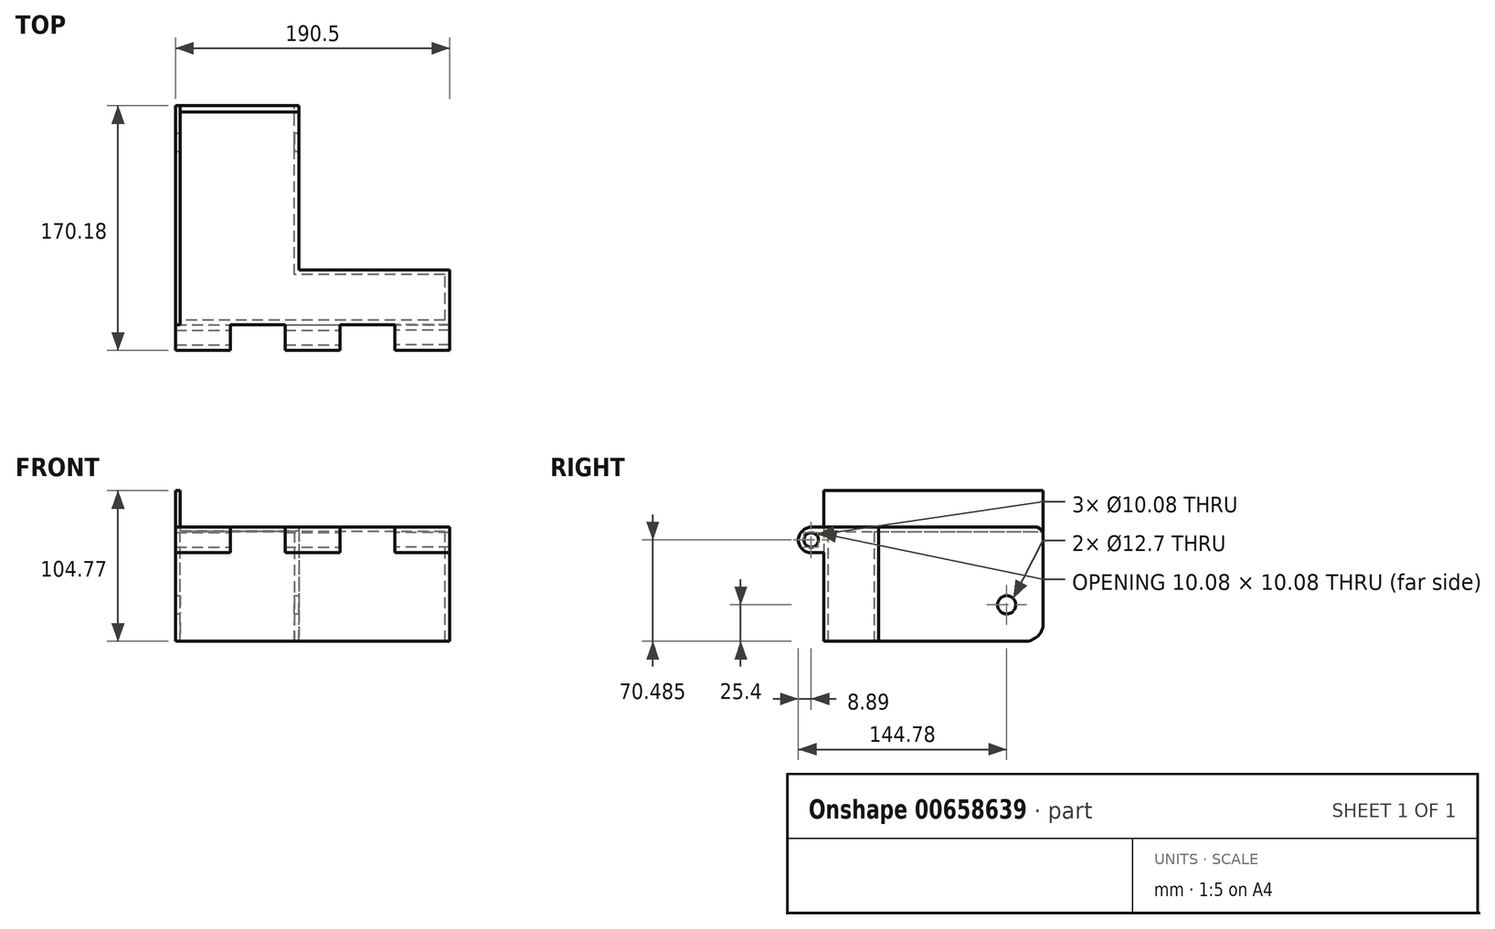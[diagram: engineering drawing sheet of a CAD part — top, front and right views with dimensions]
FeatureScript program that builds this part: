
annotation { "Feature Type Name" : "Feature", "Feature Type Description" : "" }
export const myFeature = defineFeature(function(context is Context, id is Id, definition is map)
    precondition{}
    {
        {
            var Q0;
            Q0=qCreatedBy(makeId("Front.planeOp"),FACE);
            var sketch = newSketch(context, id + "F0", { "sketchPlane" : qUnion([Q0])});
            skLineSegment(sketch, "E0.bottom", {"start": v(0, 0) * mm, "end": v(3.18, 0) * mm});
            skLineSegment(sketch, "E0.top", {"start": v(0, 76.2) * mm, "end": v(3.17, 76.2) * mm});
            skLineSegment(sketch, "E0.left", {"start": v(0, 0) * mm, "end": v(0, 76.2) * mm});
            skLineSegment(sketch, "E0.right", {"start": v(3.18, 0) * mm, "end": v(3.17, 76.2) * mm});
            skLineSegment(sketch, "E1.bottom", {"start": v(3.17, 76.2) * mm, "end": v(82.55, 76.2) * mm});
            skLineSegment(sketch, "E1.top", {"start": v(3.17, 79.38) * mm, "end": v(82.55, 79.38) * mm});
            skLineSegment(sketch, "E1.left", {"start": v(3.17, 76.2) * mm, "end": v(3.17, 79.38) * mm});
            skLineSegment(sketch, "E1.right", {"start": v(82.55, 76.2) * mm, "end": v(82.55, 79.38) * mm});
            skLineSegment(sketch, "E2.bottom", {"start": v(82.55, 76.2) * mm, "end": v(85.72, 76.2) * mm});
            skLineSegment(sketch, "E2.top", {"start": v(82.55, 0) * mm, "end": v(85.72, 0) * mm});
            skLineSegment(sketch, "E2.left", {"start": v(82.55, 76.2) * mm, "end": v(82.55, 0) * mm});
            skLineSegment(sketch, "E2.right", {"start": v(85.72, 76.2) * mm, "end": v(85.72, 0) * mm});
            skLineSegment(sketch, "E3.top", {"start": v(0, 79.38) * mm, "end": v(3.17, 79.38) * mm});
            skLineSegment(sketch, "E3.left", {"start": v(0, 76.2) * mm, "end": v(0, 79.38) * mm});
            skLineSegment(sketch, "E4.bottom", {"start": v(85.72, 76.2) * mm, "end": v(82.55, 76.2) * mm});
            skLineSegment(sketch, "E4.top", {"start": v(85.72, 79.38) * mm, "end": v(82.55, 79.38) * mm});
            skLineSegment(sketch, "E4.left", {"start": v(85.72, 76.2) * mm, "end": v(85.72, 79.38) * mm});
            skSolve(sketch);
        }
        {
            var Q0;
            Q0 = qSketchRegion(id + "F0", true);
            extrude(context, id + "F1", {"entities" : qUnion([Q0]), "depth" : 152.4 * mm, "offsetDistance" : 25.4 * mm});
        }
        {
            var Q0;
            Q0=makeQuery(id+"F1.opExtrude","SWEPT_FACE",FACE,{"disambiguationData":[OSD([sQuery(id+"F0.wireOp",EDGE,"E2.right"),sQuery(id+"F0.wireOp",EDGE,"E4.left")])]});
            var sketch = newSketch(context, id + "F2", { "sketchPlane" : qUnion([Q0])});
            skLineSegment(sketch, "E5.bottom", {"start": v(-152.4, 0) * mm, "end": v(-149.22, 0) * mm});
            skLineSegment(sketch, "E5.top", {"start": v(-152.4, 79.38) * mm, "end": v(-149.22, 79.38) * mm});
            skLineSegment(sketch, "E5.left", {"start": v(-152.4, 0) * mm, "end": v(-152.4, 79.38) * mm});
            skLineSegment(sketch, "E5.right", {"start": v(-149.22, 0) * mm, "end": v(-149.22, 79.38) * mm});
            skLineSegment(sketch, "E6", {"start": v(-152.4, 79.38) * mm, "end": v(-114.3, 79.38) * mm});
            skLineSegment(sketch, "E7.bottom", {"start": v(-114.3, 79.38) * mm, "end": v(-117.48, 79.38) * mm});
            skLineSegment(sketch, "E7.top", {"start": v(-114.3, 0) * mm, "end": v(-117.47, 0) * mm});
            skLineSegment(sketch, "E7.left", {"start": v(-114.3, 79.38) * mm, "end": v(-114.3, 0) * mm});
            skLineSegment(sketch, "E7.right", {"start": v(-117.48, 79.38) * mm, "end": v(-117.47, 0) * mm});
            skLineSegment(sketch, "E8.top", {"start": v(-152.4, 76.2) * mm, "end": v(-114.3, 76.2) * mm});
            skLineSegment(sketch, "E8.left", {"start": v(-152.4, 79.38) * mm, "end": v(-152.4, 76.2) * mm});
            skLineSegment(sketch, "E8.right", {"start": v(-114.3, 79.38) * mm, "end": v(-114.3, 76.2) * mm});
            skSolve(sketch);
        }
        {
            var Q0;
            Q0 = qSketchRegion(id + "F2", true);
            extrude(context, id + "F3", {"entities" : qUnion([Q0]), "operationType" : NewBodyOperationType.ADD, "depth" : 76.2 * mm, "offsetDistance" : 25.4 * mm});
        }
        {
            var Q0;
            Q0=makeQuery(id+"F1.opExtrude","SWEPT_FACE",FACE,{"disambiguationData":[OSD([sQuery(id+"F0.wireOp",EDGE,"E0.right")])]});
            var sketch = newSketch(context, id + "F4", { "sketchPlane" : qUnion([Q0])});
            skLineSegment(sketch, "E9.bottom", {"start": v(-152.4, 0) * mm, "end": v(-149.22, 0) * mm});
            skLineSegment(sketch, "E9.top", {"start": v(-152.4, 76.2) * mm, "end": v(-149.22, 76.2) * mm});
            skLineSegment(sketch, "E9.left", {"start": v(-152.4, 0) * mm, "end": v(-152.4, 76.2) * mm});
            skLineSegment(sketch, "E9.right", {"start": v(-149.22, 0) * mm, "end": v(-149.22, 76.2) * mm});
            skSolve(sketch);
        }
        {
            var Q0;
            Q0 = qSketchRegion(id + "F4", true);
            extrude(context, id + "F5", {"entities" : qUnion([Q0]), "operationType" : NewBodyOperationType.ADD, "endBound" : BoundingType.UP_TO_NEXT, "depth" : 25.4 * mm, "offsetDistance" : 25.4 * mm});
        }
        {
            var Q0;
            Q0=makeQuery(id+"F3.opExtrude","SWEPT_FACE",FACE,{"disambiguationData":[OSD([sQuery(id+"F2.wireOp",EDGE,"E7.right")])]});
            var sketch = newSketch(context, id + "F6", { "sketchPlane" : qUnion([Q0])});
            skLineSegment(sketch, "E10.bottom", {"start": v(161.92, 0) * mm, "end": v(158.75, 0) * mm});
            skLineSegment(sketch, "E10.top", {"start": v(161.92, 76.2) * mm, "end": v(158.75, 76.2) * mm});
            skLineSegment(sketch, "E10.left", {"start": v(161.92, 0) * mm, "end": v(161.92, 76.2) * mm});
            skLineSegment(sketch, "E10.right", {"start": v(158.75, 0) * mm, "end": v(158.75, 76.2) * mm});
            skSolve(sketch);
        }
        {
            var Q0;
            Q0 = qSketchRegion(id + "F6", true);
            extrude(context, id + "F7", {"entities" : qUnion([Q0]), "operationType" : NewBodyOperationType.ADD, "endBound" : BoundingType.UP_TO_NEXT, "depth" : 25.4 * mm, "offsetDistance" : 25.4 * mm});
        }
        {
            var Q0;
            Q0=makeQuery(id+"F7.boolean.opBoolean","MERGE",FACE,{"derivedFrom":[makeQuery(id+"F3.opExtrude","CAP_FACE",FACE,{"disambiguationData":[OSD([sQuery(id+"F2.wireOp",EDGE,"E5.bottom"),sQuery(id+"F2.wireOp",EDGE,"E5.left"),sQuery(id+"F2.wireOp",EDGE,"E5.right"),sQuery(id+"F2.wireOp",EDGE,"E7.top"),sQuery(id+"F2.wireOp",EDGE,"E7.left"),sQuery(id+"F2.wireOp",EDGE,"E7.right"),sQuery(id+"F2.wireOp",EDGE,"E6"),sQuery(id+"F2.wireOp",EDGE,"E8.top"),sQuery(id+"F2.wireOp",EDGE,"E8.left"),sQuery(id+"F2.wireOp",EDGE,"E8.right")])],"isStart":false}),makeQuery(id+"F7.opExtrude","SWEPT_FACE",FACE,{"disambiguationData":[OSD([sQuery(id+"F6.wireOp",EDGE,"E10.left")])]})]});
            var sketch = newSketch(context, id + "F8", { "sketchPlane" : qUnion([Q0])});
            skCircle(sketch, "E11", {"center": v(-161.3, 70.48) * mm, "radius": 5.04 * mm});
            skArc(sketch, "E12", {"start": v(-161.3, 79.37) * mm, "mid": v(-170.18, 70.48) * mm, "end": v(-161.3, 61.6) * mm});
            skLineSegment(sketch, "E13", {"start": v(-152.4, 79.37) * mm, "end": v(-161.3, 79.37) * mm});
            skLineSegment(sketch, "E14", {"start": v(-161.3, 61.6) * mm, "end": v(-152.4, 61.6) * mm});
            skLineSegment(sketch, "E15", {"start": v(-152.4, 61.6) * mm, "end": v(-152.4, 79.37) * mm});
            skSolve(sketch);
        }
        {
            var Q0;
            Q0 = qSketchRegion(id + "F8", true);
            var Q1;
            Q1=makeQuery(id+"F1.opExtrude","SWEPT_FACE",FACE,{"disambiguationData":[OSD([sQuery(id+"F0.wireOp",EDGE,"E0.left"),sQuery(id+"F0.wireOp",EDGE,"E3.left")])]});
            extrude(context, id + "F9", {"entities" : qUnion([Q0]), "operationType" : NewBodyOperationType.ADD, "endBound" : BoundingType.UP_TO_SURFACE, "oppositeDirection" : true, "depth" : 25.4 * mm, "endBoundEntityFace" : qUnion([Q1]), "offsetDistance" : 25.4 * mm});
        }
        {
            var Q0;
            Q0=makeQuery(id+"F9.opExtrude","SWEPT_FACE",FACE,{"disambiguationData":[OSD([sQuery(id+"F8.wireOp",EDGE,"E14")])]});
            var sketch = newSketch(context, id + "F10", { "sketchPlane" : qUnion([Q0])});
            skLineSegment(sketch, "E16.right", {"start": v(152.4, 152.4) * mm, "end": v(152.4, 171.54) * mm});
            skLineSegment(sketch, "E17.bottom", {"start": v(152.4, 171.54) * mm, "end": v(174.37, 171.54) * mm});
            skLineSegment(sketch, "E17.top", {"start": v(152.4, 103.76) * mm, "end": v(174.37, 103.76) * mm});
            skLineSegment(sketch, "E17.left", {"start": v(152.4, 171.54) * mm, "end": v(152.4, 103.76) * mm});
            skLineSegment(sketch, "E17.right", {"start": v(174.37, 171.54) * mm, "end": v(174.37, 103.76) * mm});
            skLineSegment(sketch, "E18.bottom", {"start": v(0, 152.4) * mm, "end": v(38.1, 152.4) * mm});
            skLineSegment(sketch, "E18.left", {"start": v(0, 152.4) * mm, "end": v(0, 184.67) * mm});
            skLineSegment(sketch, "E18.right", {"start": v(38.1, 152.4) * mm, "end": v(38.1, 184.67) * mm});
            skLineSegment(sketch, "E19.bottom", {"start": v(38.1, 152.4) * mm, "end": v(76.2, 152.4) * mm});
            skLineSegment(sketch, "E19.top", {"start": v(38.1, 185.65) * mm, "end": v(76.2, 185.65) * mm});
            skLineSegment(sketch, "E19.left", {"start": v(38.1, 152.4) * mm, "end": v(38.1, 185.65) * mm});
            skLineSegment(sketch, "E19.right", {"start": v(76.2, 152.4) * mm, "end": v(76.2, 185.65) * mm});
            skLineSegment(sketch, "E20.bottom", {"start": v(76.2, 152.4) * mm, "end": v(114.3, 152.4) * mm});
            skLineSegment(sketch, "E20.left", {"start": v(76.2, 152.4) * mm, "end": v(76.2, 183.56) * mm});
            skLineSegment(sketch, "E20.right", {"start": v(114.3, 152.4) * mm, "end": v(114.3, 183.56) * mm});
            skPoint(sketch, "E21.oppositeSnap0", {"position": v(152.4, 161.97) * mm});
            skLineSegment(sketch, "E21.bottom", {"start": v(114.3, 152.4) * mm, "end": v(152.4, 152.4) * mm});
            skLineSegment(sketch, "E21.top", {"start": v(114.3, 189.28) * mm, "end": v(152.4, 189.28) * mm});
            skLineSegment(sketch, "E21.left", {"start": v(114.3, 152.4) * mm, "end": v(114.3, 189.28) * mm});
            skLineSegment(sketch, "E21.right", {"start": v(152.4, 152.4) * mm, "end": v(152.4, 189.28) * mm});
            skSolve(sketch);
        }
        {
            var Q0;
            Q0 = qSketchRegion(id + "F10", true);
            extrude(context, id + "F11", {"entities" : qUnion([Q0]), "operationType" : NewBodyOperationType.REMOVE, "endBound" : BoundingType.THROUGH_ALL, "oppositeDirection" : true, "depth" : 25.4 * mm, "offsetDistance" : 25.4 * mm});
        }
        {
            var Q0;
            Q0=makeQuery(id+"F11.boolean.opBoolean","COPY",FACE,{"derivedFrom":makeQuery(id+"F11.opExtrude","CAP_FACE",FACE,{"disambiguationData":[OSD([sQuery(id+"F10.wireOp",EDGE,"E17.bottom"),sQuery(id+"F10.wireOp",EDGE,"E17.top"),sQuery(id+"F10.wireOp",EDGE,"E17.left"),sQuery(id+"F10.wireOp",EDGE,"E17.right")])],"isStart":true})});
            extrude(context, id + "F12", {"entities" : qUnion([Q0]), "operationType" : NewBodyOperationType.REMOVE, "endBound" : BoundingType.THROUGH_ALL, "oppositeDirection" : true, "depth" : 25.4 * mm, "offsetDistance" : 25.4 * mm});
        }
        {
            var Q0;
            Q0=makeQuery(id+"F9.boolean.opBoolean","MERGE",FACE,{"derivedFrom":[makeQuery(id+"F3.boolean.opBoolean","MERGE",FACE,{"derivedFrom":[makeQuery(id+"F1.opExtrude","SWEPT_FACE",FACE,{"disambiguationData":[OSD([sQuery(id+"F0.wireOp",EDGE,"E1.top"),sQuery(id+"F0.wireOp",EDGE,"E3.top"),sQuery(id+"F0.wireOp",EDGE,"E4.top")])]}),makeQuery(id+"F3.opExtrude","SWEPT_FACE",FACE,{"disambiguationData":[OSD([sQuery(id+"F2.wireOp",EDGE,"E6")])]})]}),makeQuery(id+"F9.opExtrude","SWEPT_FACE",FACE,{"disambiguationData":[OSD([sQuery(id+"F8.wireOp",EDGE,"EuQ0qAKd-v92V-Isw8-Fcm8-ui6gwBgxLgZ1")])]})]});
            var sketch = newSketch(context, id + "F13", { "sketchPlane" : qUnion([Q0])});
            skLineSegment(sketch, "E22.bottom", {"start": v(0, 0) * mm, "end": v(3.17, 0) * mm});
            skLineSegment(sketch, "E22.top", {"start": v(0, -152.4) * mm, "end": v(3.17, -152.4) * mm});
            skLineSegment(sketch, "E22.left", {"start": v(0, 0) * mm, "end": v(0, -152.4) * mm});
            skLineSegment(sketch, "E22.right", {"start": v(3.17, 0) * mm, "end": v(3.18, -152.4) * mm});
            skSolve(sketch);
        }
        {
            var Q0;
            Q0 = qSketchRegion(id + "F13", true);
            extrude(context, id + "F14", {"entities" : qUnion([Q0]), "operationType" : NewBodyOperationType.ADD, "depth" : 25.4 * mm, "offsetDistance" : 25.4 * mm});
        }
        {
            var Q0;
            Q0=makeQuery(id+"F3.boolean.opBoolean","SPLIT",FACE,{"disambiguationData":[TD([makeQuery(id+"F3.opExtrude","SWEPT_FACE",FACE,{"disambiguationData":[OSD([sQuery(id+"F2.wireOp",EDGE,"E5.right")])]})])],"derivedFrom":makeQuery(id+"F1.opExtrude","SWEPT_FACE",FACE,{"disambiguationData":[OSD([sQuery(id+"F0.wireOp",EDGE,"E2.right"),sQuery(id+"F0.wireOp",EDGE,"E4.left")])]})});
            extrude(context, id + "F15", {"entities" : qUnion([Q0]), "operationType" : NewBodyOperationType.REMOVE, "oppositeDirection" : true, "depth" : 25.4 * mm, "offsetDistance" : 25.4 * mm});
        }
        {
            var Q0;
            {var subQ0=sQuery(id+"F0.wireOp",EDGE,"E4.left");var subQ3=sQuery(id+"F0.wireOp",EDGE,"E2.right");Q0=makeQuery(id+"F3.boolean.opBoolean","SPLIT",FACE,{"disambiguationData":[TD([makeQuery(id+"F3.opExtrude","SWEPT_FACE",FACE,{"disambiguationData":[OSD([sQuery(id+"F2.wireOp",EDGE,"E6")])]})])],"derivedFrom":makeQuery(id+"F1.opExtrude","SWEPT_FACE",FACE,{"disambiguationData":[OSD([subQ3,subQ0])]})});}
            var sketch = newSketch(context, id + "F16", { "sketchPlane" : qUnion([Q0])});
            skCircle(sketch, "E23", {"center": v(-25.4, 25.4) * mm, "radius": 6.35 * mm});
            skSolve(sketch);
        }
        {
            var Q0;
            Q0=makeQuery(id+"F16.imprint","IMPRINT",FACE,{"disambiguationData":[TD([[makeQuery(id+"F16.imprint","IMPRINT",EDGE,{"derivedFrom":sQuery(id+"F16.wireOp",EDGE,"E23")}),1.0]])]});
            extrude(context, id + "F17", {"entities" : qUnion([Q0]), "operationType" : NewBodyOperationType.REMOVE, "endBound" : BoundingType.THROUGH_ALL, "oppositeDirection" : true, "depth" : 25.4 * mm, "offsetDistance" : 25.4 * mm});
        }
        {
            var Q0;
            Q0=makeQuery(id+"F1.opExtrude","CAP_EDGE",EDGE,{"disambiguationData":[OSD([sQuery(id+"F0.wireOp",EDGE,"E2.top")])],"isStart":true});
            var Q1;
            Q1=makeQuery(id+"F1.opExtrude","CAP_EDGE",EDGE,{"disambiguationData":[OSD([sQuery(id+"F0.wireOp",EDGE,"E0.bottom")])],"isStart":true});
            fillet(context, id + "F18", {"entities" : qUnion([Q0, Q1]), "radius" : 12.7 * mm, "tangentPropagation" : true, "allowEdgeOverflow" : false});
        }
        {
            var Q0;
            Q0=makeQuery(id+"F1.opExtrude","CAP_EDGE",EDGE,{"disambiguationData":[OSD([sQuery(id+"F0.wireOp",EDGE,"E1.top"),sQuery(id+"F0.wireOp",EDGE,"E3.top"),sQuery(id+"F0.wireOp",EDGE,"E4.top")])],"isStart":true});
            chamfer(context, id + "F19", {"entities" : qUnion([Q0]), "chamferType" : ChamferType.OFFSET_ANGLE, "width" : 2.54 * mm, "oppositeDirection" : false, "angle" : 60 * degree, "tangentPropagation" : true});
        }
        {
            var Q0;
            {var subQ1=sQuery(id+"F10.wireOp",EDGE,"E17.left");var subQ3=makeQuery(id+"F11.opExtrude","SWEPT_FACE",FACE,{"disambiguationData":[OSD([subQ1])]});var subQ4=makeQuery(id+"F11.opExtrude","CAP_EDGE",EDGE,{"disambiguationData":[OSD([subQ1])],"isStart":true});Q0=makeQuery(id+"F12.boolean.opBoolean","MERGE",FACE,{"derivedFrom":[makeQuery(id+"F11.boolean.opBoolean","COPY",FACE,{"derivedFrom":subQ3}),makeQuery(id+"F12.opExtrude","SWEPT_FACE",FACE,{"disambiguationData":[OSD([subQ1]),TDD([makeQuery(id+"F11.boolean.opBoolean","COPY",EDGE,{"disambiguationData":[TD([makeQuery(id+"F3.opExtrude","SWEPT_FACE",FACE,{"disambiguationData":[OSD([sQuery(id+"F2.wireOp",EDGE,"E5.right")])]})])],"derivedFrom":subQ4})])]}),makeQuery(id+"F12.opExtrude","SWEPT_FACE",FACE,{"disambiguationData":[OSD([subQ1]),TDD([makeQuery(id+"F11.boolean.opBoolean","COPY",EDGE,{"disambiguationData":[TD([makeQuery(id+"F3.opExtrude","SWEPT_FACE",FACE,{"disambiguationData":[OSD([sQuery(id+"F2.wireOp",EDGE,"E7.right")])]})])],"derivedFrom":subQ4})])]})]});}
            extrude(context, id + "F20", {"entities" : qUnion([Q0]), "operationType" : NewBodyOperationType.ADD, "depth" : 38.1 * mm, "offsetDistance" : 25.4 * mm});
        }
        {
            var Q0;
            {var subQ0=sQuery(id+"F2.wireOp",EDGE,"E7.right");Q0=makeQuery(id+"F20.boolean.opBoolean","MERGE",FACE,{"derivedFrom":[makeQuery(id+"F15.boolean.opBoolean","MERGE",FACE,{"derivedFrom":[makeQuery(id+"F3.opExtrude","SWEPT_FACE",FACE,{"disambiguationData":[OSD([subQ0])]}),makeQuery(id+"F15.opExtrude","SWEPT_FACE",FACE,{"disambiguationData":[OSD([subQ0])]})]}),makeQuery(id+"F20.opExtrude","SWEPT_FACE",FACE,{"disambiguationData":[OSD([subQ0,sQuery(id+"F10.wireOp",EDGE,"E17.bottom"),sQuery(id+"F10.wireOp",EDGE,"E17.top"),sQuery(id+"F10.wireOp",EDGE,"E17.left"),sQuery(id+"F10.wireOp",EDGE,"E17.right"),sQuery(id+"F10.wireOp",EDGE,"E21.bottom"),sQuery(id+"F10.wireOp",EDGE,"E21.top"),sQuery(id+"F10.wireOp",EDGE,"E21.left"),sQuery(id+"F10.wireOp",EDGE,"E21.right")])]})]});}
            var sketch = newSketch(context, id + "F21", { "sketchPlane" : qUnion([Q0])});
            skLineSegment(sketch, "E24.bottom", {"start": v(190.5, 0) * mm, "end": v(187.33, 0) * mm});
            skLineSegment(sketch, "E24.top", {"start": v(190.5, 76.2) * mm, "end": v(187.33, 76.2) * mm});
            skLineSegment(sketch, "E24.left", {"start": v(190.5, 0) * mm, "end": v(190.5, 76.2) * mm});
            skLineSegment(sketch, "E24.right", {"start": v(187.33, 0) * mm, "end": v(187.33, 76.2) * mm});
            skSolve(sketch);
        }
        {
            var Q0;
            Q0=makeQuery(id+"F21.imprint","IMPRINT",FACE,{"disambiguationData":[TD([[makeQuery(id+"F21.imprint","IMPRINT",EDGE,{"derivedFrom":sQuery(id+"F21.wireOp",EDGE,"E24.bottom")}),-1.0]])]});
            extrude(context, id + "F22", {"entities" : qUnion([Q0]), "operationType" : NewBodyOperationType.ADD, "endBound" : BoundingType.UP_TO_NEXT, "depth" : 25.4 * mm, "offsetDistance" : 25.4 * mm});
        }
        {
            var Q0;
            Q0 = qSketchRegion(id + "F8", true);
            var Q1;
            Q1=makeQuery(id+"F22.boolean.opBoolean","MERGE",FACE,{"derivedFrom":[makeQuery(id+"F20.opExtrude","CAP_FACE",FACE,{"disambiguationData":[OSD([sQuery(id+"F10.wireOp",EDGE,"E17.left")])],"isStart":false}),makeQuery(id+"F22.opExtrude","SWEPT_FACE",FACE,{"disambiguationData":[OSD([sQuery(id+"F21.wireOp",EDGE,"E24.left")])]})]});
            extrude(context, id + "F23", {"entities" : qUnion([Q0]), "operationType" : NewBodyOperationType.ADD, "endBound" : BoundingType.UP_TO_SURFACE, "depth" : 25.4 * mm, "endBoundEntityFace" : qUnion([Q1]), "offsetDistance" : 25.4 * mm});
        }
        {
            var Q0;
            Q0=makeQuery(id+"F23.opExtrude","CAP_FACE",FACE,{"disambiguationData":[OSD([sQuery(id+"F8.wireOp",EDGE,"E11"),sQuery(id+"F8.wireOp",EDGE,"E12"),sQuery(id+"F8.wireOp",EDGE,"E13"),sQuery(id+"F8.wireOp",EDGE,"E14"),sQuery(id+"F8.wireOp",EDGE,"E15")])],"isStart":true});
            extrude(context, id + "F24", {"entities" : qUnion([Q0]), "operationType" : NewBodyOperationType.ADD, "depth" : 9.52 * mm, "offsetDistance" : 25.4 * mm});
        }
    });
